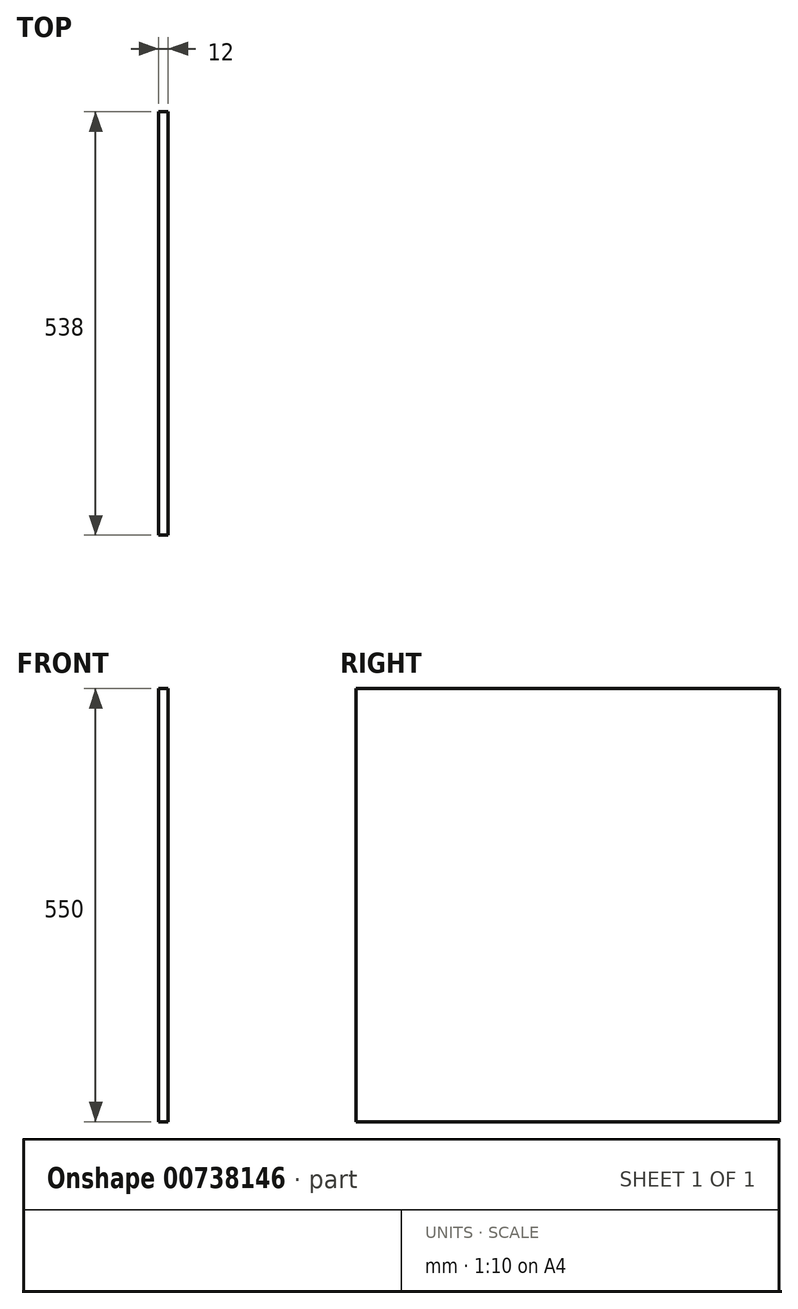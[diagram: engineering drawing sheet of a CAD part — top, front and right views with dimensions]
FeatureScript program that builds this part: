
annotation { "Feature Type Name" : "Feature", "Feature Type Description" : "" }
export const myFeature = defineFeature(function(context is Context, id is Id, definition is map)
    precondition{}
    {
        {
            var Q0;
            Q0=qCreatedBy(makeId("Right.planeOp"),FACE);
            var sketch = newSketch(context, id + "F0", { "sketchPlane" : qUnion([Q0])});
            skLineSegment(sketch, "E0.bottom", {"start": v(-269, -275) * mm, "end": v(269, -275) * mm});
            skLineSegment(sketch, "E0.top", {"start": v(-269, 275) * mm, "end": v(269, 275) * mm});
            skLineSegment(sketch, "E0.left", {"start": v(-269, -275) * mm, "end": v(-269, 275) * mm});
            skLineSegment(sketch, "E0.right", {"start": v(269, -275) * mm, "end": v(269, 275) * mm});
            skPoint(sketch, "E0.middle", {"position": v(0, 0) * mm});
            skSolve(sketch);
        }
        {
            var Q0;
            Q0 = qSketchRegion(id + "F0", true);
            extrude(context, id + "F1", {"entities" : qUnion([Q0]), "depth" : 12 * mm, "offsetDistance" : 25 * mm});
        }
    });
